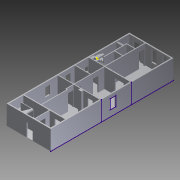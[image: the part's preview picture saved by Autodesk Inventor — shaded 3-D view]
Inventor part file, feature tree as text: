
AUTODESK INVENTOR PART (.ipt)
format: ipt  version: 2013 SP2 (Build 170200200, 200)  size: 349,184 bytes
history: native  units: in
note: dims shown in document units (in); Inventor stores cm internally (conversion verified against a paired STEP export)
features: sketch x3, other x1, extrude x1, imported_body x1
ambient origin geometry x8: Origin, YZ Plane, XZ Plane, XY Plane, X Axis, Y Axis, Z Axis, Center Point
feature tree (6):
  other  "1st Floor1"
  extrude  "Extrusion1"  [1 undecoded]
  sketch  "Sketch2"
  sketch  "3D Sketch1"
  imported_body  "Base1"
  sketch  "Sketch1"  dims[d0=5.5in d1=0.0in]
note: 1 required parameter value undecoded (feature->parameter linkage not recoverable at this tier; creation-order binding heuristic only, values carry confidence <= 0.55)
